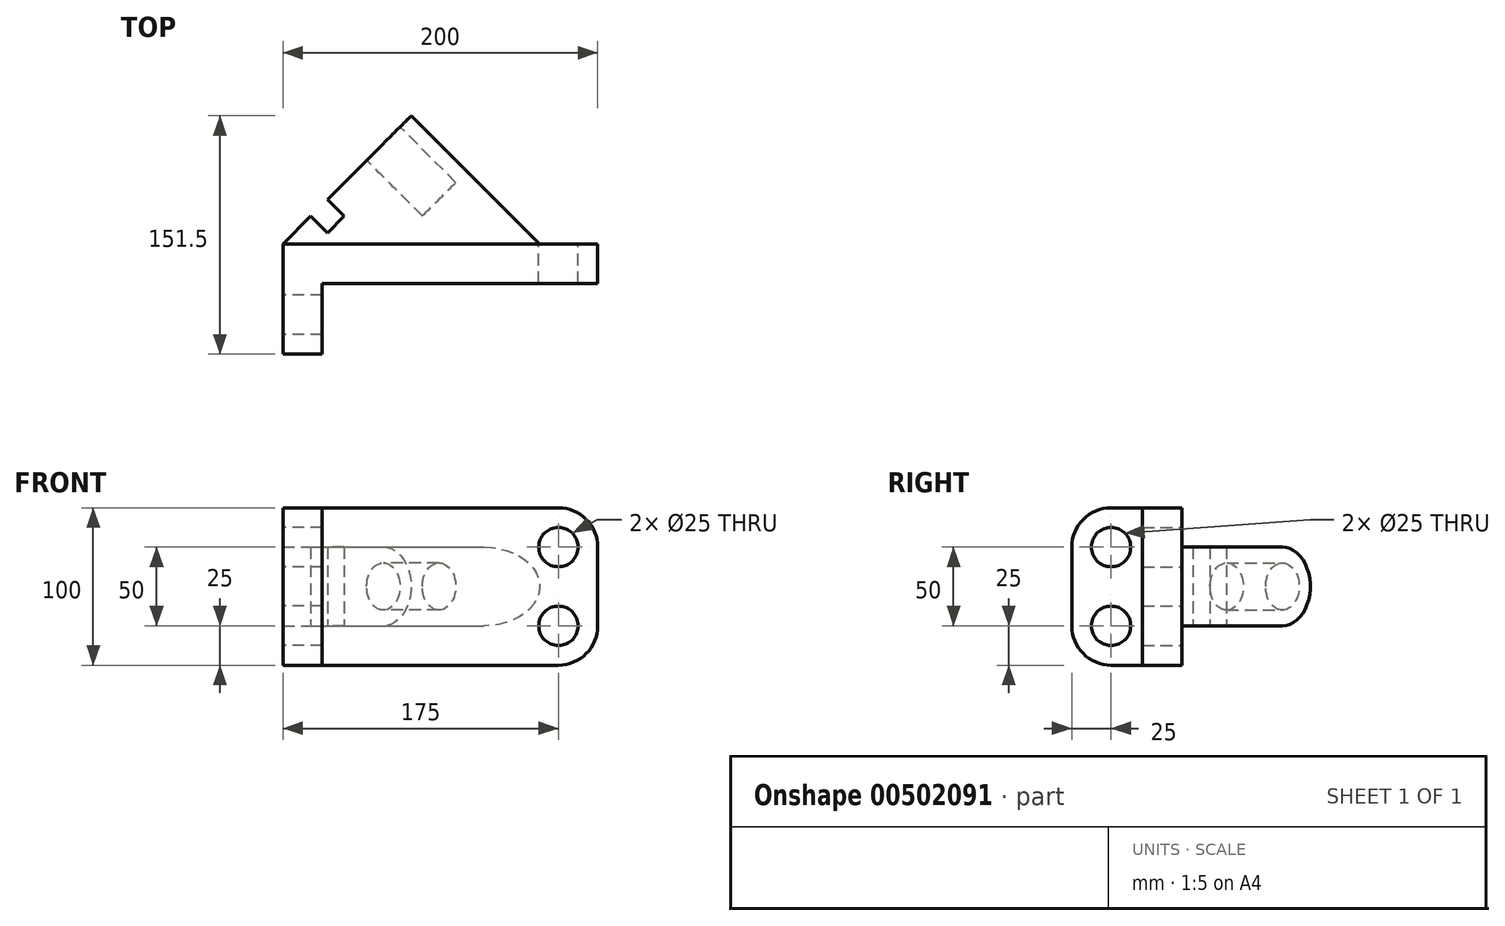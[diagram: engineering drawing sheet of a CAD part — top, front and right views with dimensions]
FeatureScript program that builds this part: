
annotation { "Feature Type Name" : "Feature", "Feature Type Description" : "" }
export const myFeature = defineFeature(function(context is Context, id is Id, definition is map)
    precondition{}
    {
        {
            var Q0;
            Q0=qCreatedBy(makeId("Top.planeOp"),FACE);
            var sketch = newSketch(context, id + "F0", { "sketchPlane" : qUnion([Q0])});
            skLineSegment(sketch, "E0.bottom", {"start": v(0, 0) * mm, "end": v(25, 0) * mm});
            skLineSegment(sketch, "E0.top", {"start": v(0, 70) * mm, "end": v(200, 70) * mm});
            skLineSegment(sketch, "E0.left", {"start": v(0, 0) * mm, "end": v(0, 70) * mm});
            skLineSegment(sketch, "E0.right", {"start": v(200, 45) * mm, "end": v(200, 70) * mm});
            skLineSegment(sketch, "E1.top", {"start": v(25, 45) * mm, "end": v(200, 45) * mm});
            skLineSegment(sketch, "E1.left", {"start": v(25, 0) * mm, "end": v(25, 45) * mm});
            skLineSegment(sketch, "E2", {"start": v(0, 70) * mm, "end": v(17.68, 87.68) * mm});
            skLineSegment(sketch, "E3", {"start": v(81.5, 151.5) * mm, "end": v(163, 70) * mm});
            skLineSegment(sketch, "E4", {"start": v(17.68, 87.68) * mm, "end": v(28.28, 77.07) * mm});
            skLineSegment(sketch, "E5", {"start": v(28.28, 77.07) * mm, "end": v(38.9, 87.68) * mm});
            skLineSegment(sketch, "E6", {"start": v(38.9, 87.68) * mm, "end": v(28.28, 98.28) * mm});
            skLineSegment(sketch, "E7.trimOffspring", {"start": v(28.28, 98.28) * mm, "end": v(81.5, 151.5) * mm});
            skSolve(sketch);
        }
        {
            var Q0;
            Q0=makeQuery(id+"F0.imprint","IMPRINT",FACE,{"disambiguationData":[TD([[makeQuery(id+"F0.imprint","IMPRINT",EDGE,{"derivedFrom":sQuery(id+"F0.wireOp",EDGE,"E0.bottom")}),1.0]])]});
            extrude(context, id + "F1", {"entities" : qUnion([Q0]), "depth" : 100 * mm, "offsetDistance" : 25 * mm});
        }
        {
            var Q0;
            Q0=makeQuery(id+"F1.opExtrude","CAP_EDGE",EDGE,{"disambiguationData":[OSD([sQuery(id+"F0.wireOp",EDGE,"E0.right")])],"isStart":false});
            var Q1;
            Q1=makeQuery(id+"F1.opExtrude","CAP_EDGE",EDGE,{"disambiguationData":[OSD([sQuery(id+"F0.wireOp",EDGE,"E0.right")])],"isStart":true});
            var Q2;
            Q2=makeQuery(id+"F1.opExtrude","CAP_EDGE",EDGE,{"disambiguationData":[OSD([sQuery(id+"F0.wireOp",EDGE,"E0.bottom")])],"isStart":false});
            var Q3;
            Q3=makeQuery(id+"F1.opExtrude","CAP_EDGE",EDGE,{"disambiguationData":[OSD([sQuery(id+"F0.wireOp",EDGE,"E0.bottom")])],"isStart":true});
            fillet(context, id + "F2", {"entities" : qUnion([Q0, Q1, Q2, Q3]), "radius" : 25 * mm, "tangentPropagation" : true, "allowEdgeOverflow" : false});
        }
        {
            var Q0;
            {var subQ1=sQuery(id+"F0.wireOp",EDGE,"E2");Q0=makeQuery(id+"F0.imprint","IMPRINT",FACE,{"disambiguationData":[TD([[makeQuery(id+"F0.imprint","IMPRINT",EDGE,{"derivedFrom":subQ1}),-1.0]])]});}
            extrude(context, id + "F3", {"entities" : qUnion([Q0]), "operationType" : NewBodyOperationType.ADD, "depth" : 75 * mm, "offsetDistance" : 25 * mm, "hasSecondDirection" : true, "secondDirectionOppositeDirection" : false, "secondDirectionDepth" : 25 * mm});
        }
        {
            var Q0;
            Q0=makeQuery(id+"F3.opExtrude","CAP_EDGE",EDGE,{"disambiguationData":[OSD([sQuery(id+"F0.wireOp",EDGE,"E3")])],"isStart":false});
            var Q1;
            Q1=makeQuery(id+"F3.opExtrude","CAP_EDGE",EDGE,{"disambiguationData":[OSD([sQuery(id+"F0.wireOp",EDGE,"E3")])],"isStart":true});
            fillet(context, id + "F4", {"entities" : qUnion([Q0, Q1]), "radius" : 25 * mm, "tangentPropagation" : true, "allowEdgeOverflow" : false});
        }
        {
            var Q0;
            Q0=makeQuery(id+"F1.opExtrude","SWEPT_FACE",FACE,{"disambiguationData":[OSD([sQuery(id+"F0.wireOp",EDGE,"E0.top")])]});
            var sketch = newSketch(context, id + "F5", { "sketchPlane" : qUnion([Q0])});
            skPoint(sketch, "E8", {"position": v(-175, 25) * mm});
            skPoint(sketch, "E9", {"position": v(-175, 75) * mm});
            skSolve(sketch);
        }
        {
            var Q0;
            Q0=sQuery(id+"F5.wireOp",VERTEX,"E8");
            var Q1;
            Q1=sQuery(id+"F5.wireOp",VERTEX,"E9");
            var Q2;
            Q2=makeQuery(id+"F1.opExtrude","SWEPT_BODY",BODY,{"disambiguationData":[OSD([sQuery(id+"F0.wireOp",EDGE,"E0.bottom"),sQuery(id+"F0.wireOp",EDGE,"E0.top"),sQuery(id+"F0.wireOp",EDGE,"E0.left"),sQuery(id+"F0.wireOp",EDGE,"E0.right"),sQuery(id+"F0.wireOp",EDGE,"E1.top"),sQuery(id+"F0.wireOp",EDGE,"E1.left")])]});
            hole(context, id + "F6", {"style" : HoleStyle.SIMPLE, "endStyle" : HoleEndStyle.BLIND, "holeDiameter" : 25 * mm, "majorDiameter" : 5 * mm, "holeDepth" : 195 * mm, "isTappedThrough" : true, "tappedDepth" : 12 * mm, "tapClearance" : 3, "locations" : qUnion([Q0, Q1]), "scope" : qUnion([Q2])});
        }
        {
            var Q0;
            Q0=makeQuery(id+"F1.opExtrude","SWEPT_FACE",FACE,{"disambiguationData":[OSD([sQuery(id+"F0.wireOp",EDGE,"E0.left")])]});
            var sketch = newSketch(context, id + "F7", { "sketchPlane" : qUnion([Q0])});
            skPoint(sketch, "E10", {"position": v(-25, 25) * mm});
            skPoint(sketch, "E11", {"position": v(-25, 75) * mm});
            skSolve(sketch);
        }
        {
            var Q0;
            Q0=sQuery(id+"F7.wireOp",VERTEX,"E10");
            var Q1;
            Q1=sQuery(id+"F7.wireOp",VERTEX,"E11");
            var Q2;
            Q2=makeQuery(id+"F1.opExtrude","SWEPT_BODY",BODY,{"disambiguationData":[OSD([sQuery(id+"F0.wireOp",EDGE,"E0.bottom"),sQuery(id+"F0.wireOp",EDGE,"E0.top"),sQuery(id+"F0.wireOp",EDGE,"E0.left"),sQuery(id+"F0.wireOp",EDGE,"E0.right"),sQuery(id+"F0.wireOp",EDGE,"E1.top"),sQuery(id+"F0.wireOp",EDGE,"E1.left")])]});
            hole(context, id + "F8", {"style" : HoleStyle.SIMPLE, "endStyle" : HoleEndStyle.BLIND, "holeDiameter" : 25 * mm, "majorDiameter" : 5 * mm, "holeDepth" : 195 * mm, "isTappedThrough" : true, "tappedDepth" : 12 * mm, "tapClearance" : 3, "locations" : qUnion([Q0, Q1]), "scope" : qUnion([Q2])});
        }
        {
            var Q0;
            Q0=makeQuery(id+"F3.opExtrude","SWEPT_FACE",FACE,{"disambiguationData":[OSD([sQuery(id+"F0.wireOp",EDGE,"E7.trimOffspring")])]});
            var sketch = newSketch(context, id + "F9", { "sketchPlane" : qUnion([Q0])});
            skPoint(sketch, "E12", {"position": v(-139.76, 50) * mm});
            skCircle(sketch, "E13", {"center": v(-139.76, 50) * mm, "radius": 15 * mm});
            skSolve(sketch);
        }
        {
            var Q0;
            Q0=makeQuery(id+"F9.imprint","IMPRINT",FACE,{"disambiguationData":[TD([[makeQuery(id+"F9.imprint","IMPRINT",EDGE,{"derivedFrom":sQuery(id+"F9.wireOp",EDGE,"E13")}),1.0]])]});
            extrude(context, id + "F10", {"entities" : qUnion([Q0]), "operationType" : NewBodyOperationType.REMOVE, "oppositeDirection" : true, "depth" : 50 * mm, "offsetDistance" : 25 * mm});
        }
    });
